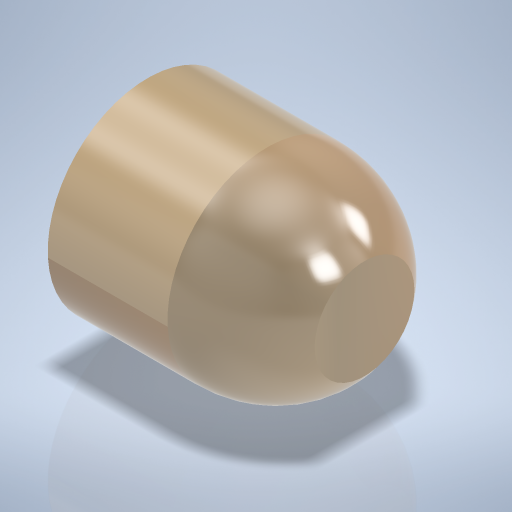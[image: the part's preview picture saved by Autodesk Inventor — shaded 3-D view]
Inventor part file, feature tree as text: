
AUTODESK INVENTOR PART (.ipt)
format: ipt  version: 2024 (Build 280153000, 153)  size: 288,256 bytes
history: native  units: mm
features: sketch x2, revolve x1, extrude x1
ambient origin geometry x8: Origin, YZ Plane, XZ Plane, XY Plane, X Axis, Y Axis, Z Axis, Center Point
bodies: Volumenkörper1 (feature_tree)
feature tree (4):
  revolve  "Umdrehung1"
  extrude  "Extrusion1"  Depth=3.0mm
  sketch  "Skizze1"  dims[d1=2.5mm d2=3.0mm]
  sketch  "Skizze2"  dims[d3=3.0mm d5=5.436699mm d6=90.0deg d7=1.61mm d8=4.0mm d9=0.0mm]
